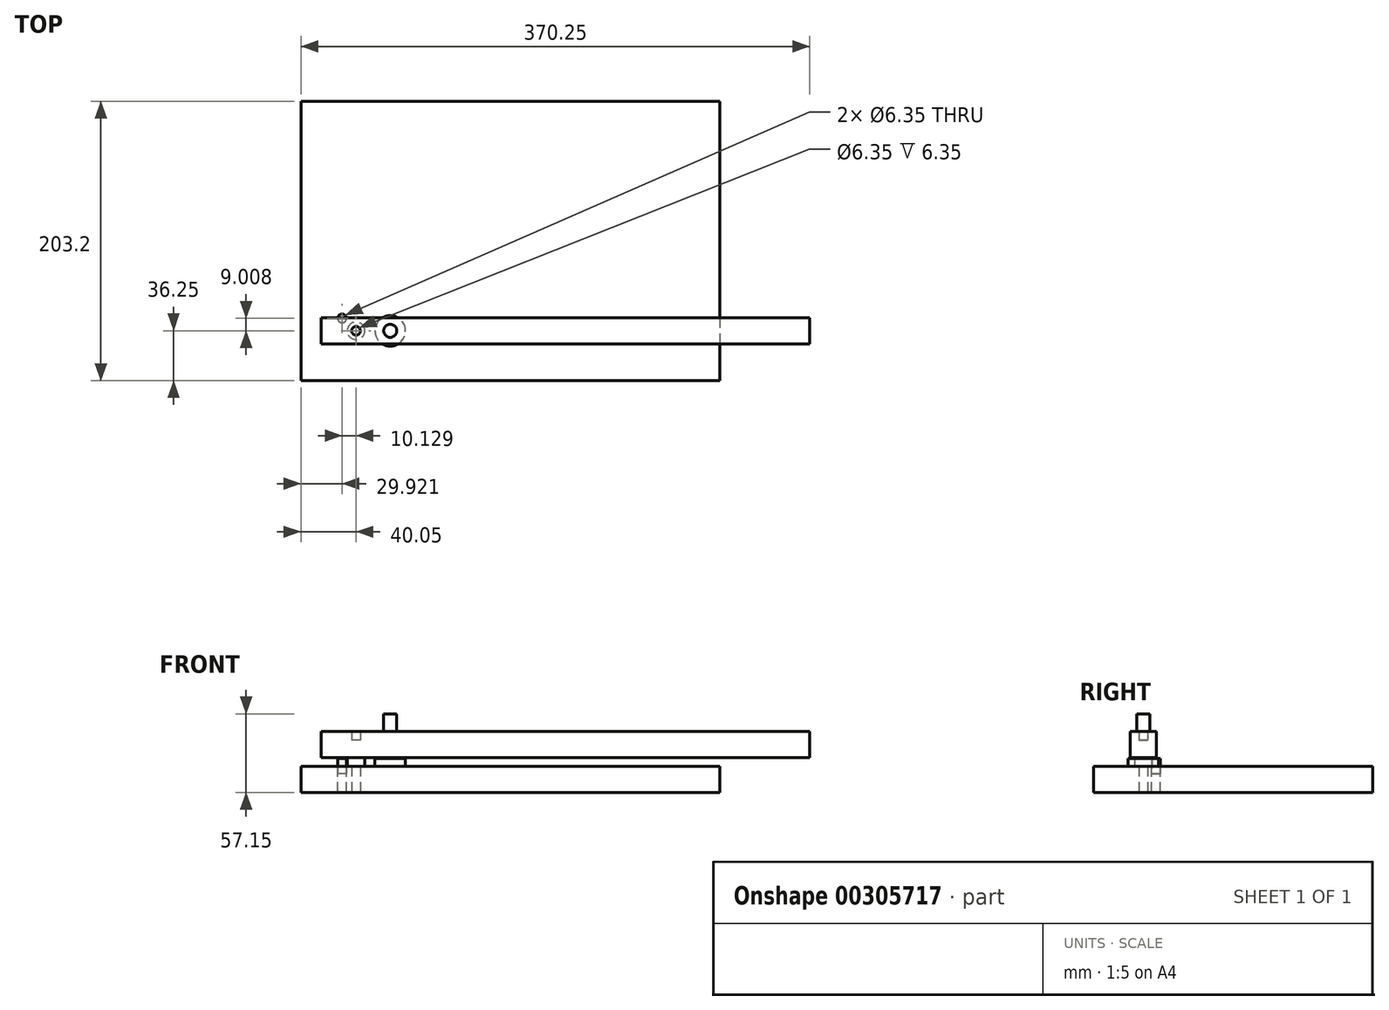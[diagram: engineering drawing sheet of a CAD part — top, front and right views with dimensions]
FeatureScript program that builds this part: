
annotation { "Feature Type Name" : "Feature", "Feature Type Description" : "" }
export const myFeature = defineFeature(function(context is Context, id is Id, definition is map)
    precondition{}
    {
        {
            var Q0;
            Q0=qCreatedBy(makeId("Top.planeOp"),FACE);
            var sketch = newSketch(context, id + "F0", { "sketchPlane" : qUnion([Q0])});
            skCircle(sketch, "E0", {"center": v(0, 0) * mm, "radius": 3.18 * mm});
            skCircle(sketch, "E1", {"center": v(0, 0) * mm, "radius": 6.35 * mm});
            skCircle(sketch, "E2", {"center": v(24.9, 0) * mm, "radius": 4.76 * mm});
            skCircle(sketch, "E3", {"center": v(24.9, 0) * mm, "radius": 11.11 * mm});
            skCircle(sketch, "E4", {"center": v(-10.16, 9.06) * mm, "radius": 3.18 * mm});
            skSolve(sketch);
        }
        {
            var Q0;
            Q0=makeQuery(id+"F0.imprint","IMPRINT",FACE,{"disambiguationData":[TD([[makeQuery(id+"F0.imprint","IMPRINT",EDGE,{"derivedFrom":sQuery(id+"F0.wireOp",EDGE,"E0")}),1.0]])]});
            var Q1;
            Q1=sQuery(id+"F0.wireOp",EDGE,"E2");
            var Q2;
            Q2=sQuery(id+"F0.wireOp",EDGE,"E0");
            extrude(context, id + "F1", {"entities" : qUnion([Q0]), "surfaceEntities" : qUnion([Q1, Q2]), "depth" : 38.1 * mm, "symmetric" : true});
        }
        {
            var Q0;
            Q0=makeQuery(id+"F0.imprint","IMPRINT",FACE,{"disambiguationData":[TD([[makeQuery(id+"F0.imprint","IMPRINT",EDGE,{"derivedFrom":sQuery(id+"F0.wireOp",EDGE,"E4")}),1.0]])]});
            var Q1;
            Q1=sQuery(id+"F0.wireOp",EDGE,"E4");
            extrude(context, id + "F2", {"entities" : qUnion([Q0]), "surfaceEntities" : qUnion([Q1]), "depth" : 11.1 * mm, "symmetric" : true});
        }
        {
            var Q0;
            Q0=makeQuery(id+"F0.imprint","IMPRINT",FACE,{"disambiguationData":[TD([[makeQuery(id+"F0.imprint","IMPRINT",EDGE,{"derivedFrom":sQuery(id+"F0.wireOp",EDGE,"E0")}),-1.0]])]});
            var Q1;
            Q1=sQuery(id+"F0.wireOp",EDGE,"E1");
            extrude(context, id + "F3", {"entities" : qUnion([Q0]), "surfaceEntities" : qUnion([Q1]), "depth" : 6.35 * mm});
        }
        {
            var Q0;
            Q0=makeQuery(id+"F0.imprint","IMPRINT",FACE,{"disambiguationData":[TD([[makeQuery(id+"F0.imprint","IMPRINT",EDGE,{"derivedFrom":sQuery(id+"F0.wireOp",EDGE,"E2")}),-1.0]])]});
            var Q1;
            Q1=sQuery(id+"F0.wireOp",EDGE,"E3");
            extrude(context, id + "F4", {"entities" : qUnion([Q0]), "surfaceEntities" : qUnion([Q1]), "depth" : 5.56 * mm});
        }
        {
            var Q0;
            Q0=makeQuery(id+"F0.imprint","IMPRINT",FACE,{"disambiguationData":[TD([[makeQuery(id+"F0.imprint","IMPRINT",EDGE,{"derivedFrom":sQuery(id+"F0.wireOp",EDGE,"E2")}),1.0]])]});
            extrude(context, id + "F5", {"entities" : qUnion([Q0]), "operationType" : NewBodyOperationType.ADD, "depth" : 38.1 * mm});
        }
        {
            var Q0;
            Q0=qCreatedBy(makeId("Top.planeOp"),FACE);
            var sketch = newSketch(context, id + "F6", { "sketchPlane" : qUnion([Q0])});
            skLineSegment(sketch, "E5.bottom", {"start": v(-40.05, 166.95) * mm, "end": v(264.75, 166.95) * mm});
            skLineSegment(sketch, "E5.top", {"start": v(-40.05, -36.25) * mm, "end": v(264.75, -36.25) * mm});
            skLineSegment(sketch, "E5.left", {"start": v(-40.05, 166.95) * mm, "end": v(-40.05, -36.25) * mm});
            skLineSegment(sketch, "E5.right", {"start": v(264.75, 166.95) * mm, "end": v(264.75, -36.25) * mm});
            skCircle(sketch, "E6", {"center": v(0, 0) * mm, "radius": 3.18 * mm});
            skCircle(sketch, "E7", {"center": v(-10.13, 9) * mm, "radius": 3.18 * mm});
            skSolve(sketch);
        }
        {
            var Q0;
            Q0=makeQuery(id+"F6.imprint","IMPRINT",FACE,{"disambiguationData":[TD([[makeQuery(id+"F6.imprint","IMPRINT",EDGE,{"derivedFrom":sQuery(id+"F6.wireOp",EDGE,"E5.bottom")}),-1.0]])]});
            extrude(context, id + "F7", {"entities" : qUnion([Q0]), "oppositeDirection" : true, "depth" : 19.05 * mm});
        }
        {
            var Q0;
            Q0=makeQuery(id+"F3.opExtrude","CAP_FACE",FACE,{"disambiguationData":[OSD([sQuery(id+"F0.wireOp",EDGE,"E0"),sQuery(id+"F0.wireOp",EDGE,"E1")])],"isStart":false});
            var sketch = newSketch(context, id + "F8", { "sketchPlane" : qUnion([Q0])});
            skLineSegment(sketch, "E8.bottom", {"start": v(-25.4, -9.52) * mm, "end": v(25.4, -9.52) * mm});
            skLineSegment(sketch, "E8.top", {"start": v(-25.4, 9.53) * mm, "end": v(25.4, 9.53) * mm});
            skLineSegment(sketch, "E8.left", {"start": v(-25.4, -9.52) * mm, "end": v(-25.4, 9.53) * mm});
            skPoint(sketch, "E8.middle", {"position": v(0, 0) * mm});
            skLineSegment(sketch, "E9.bottom", {"start": v(25.4, -9.52) * mm, "end": v(330.2, -9.52) * mm});
            skLineSegment(sketch, "E9.top", {"start": v(25.4, 9.53) * mm, "end": v(330.2, 9.53) * mm});
            skLineSegment(sketch, "E9.right", {"start": v(330.2, -9.52) * mm, "end": v(330.2, 9.53) * mm});
            skSolve(sketch);
        }
        {
            var Q0;
            Q0=makeQuery(id+"F8.imprint","IMPRINT",FACE,{"disambiguationData":[TD([[makeQuery(id+"F8.imprint","IMPRINT",EDGE,{"derivedFrom":sQuery(id+"F8.wireOp",EDGE,"E8.bottom")}),1.0]])]});
            var Q1;
            Q1=makeQuery(id+"F8.imprint","IMPRINT",FACE,{"disambiguationData":[TD([[makeQuery(id+"F8.imprint","IMPRINT",EDGE,{"derivedFrom":makeQuery(id+"F3.opExtrude","CAP_EDGE",EDGE,{"disambiguationData":[OSD([sQuery(id+"F0.wireOp",EDGE,"E0")])],"isStart":false})}),-1.0]])]});
            extrude(context, id + "F9", {"entities" : qUnion([Q0, Q1]), "operationType" : NewBodyOperationType.ADD, "depth" : 19.05 * mm});
        }
    });
